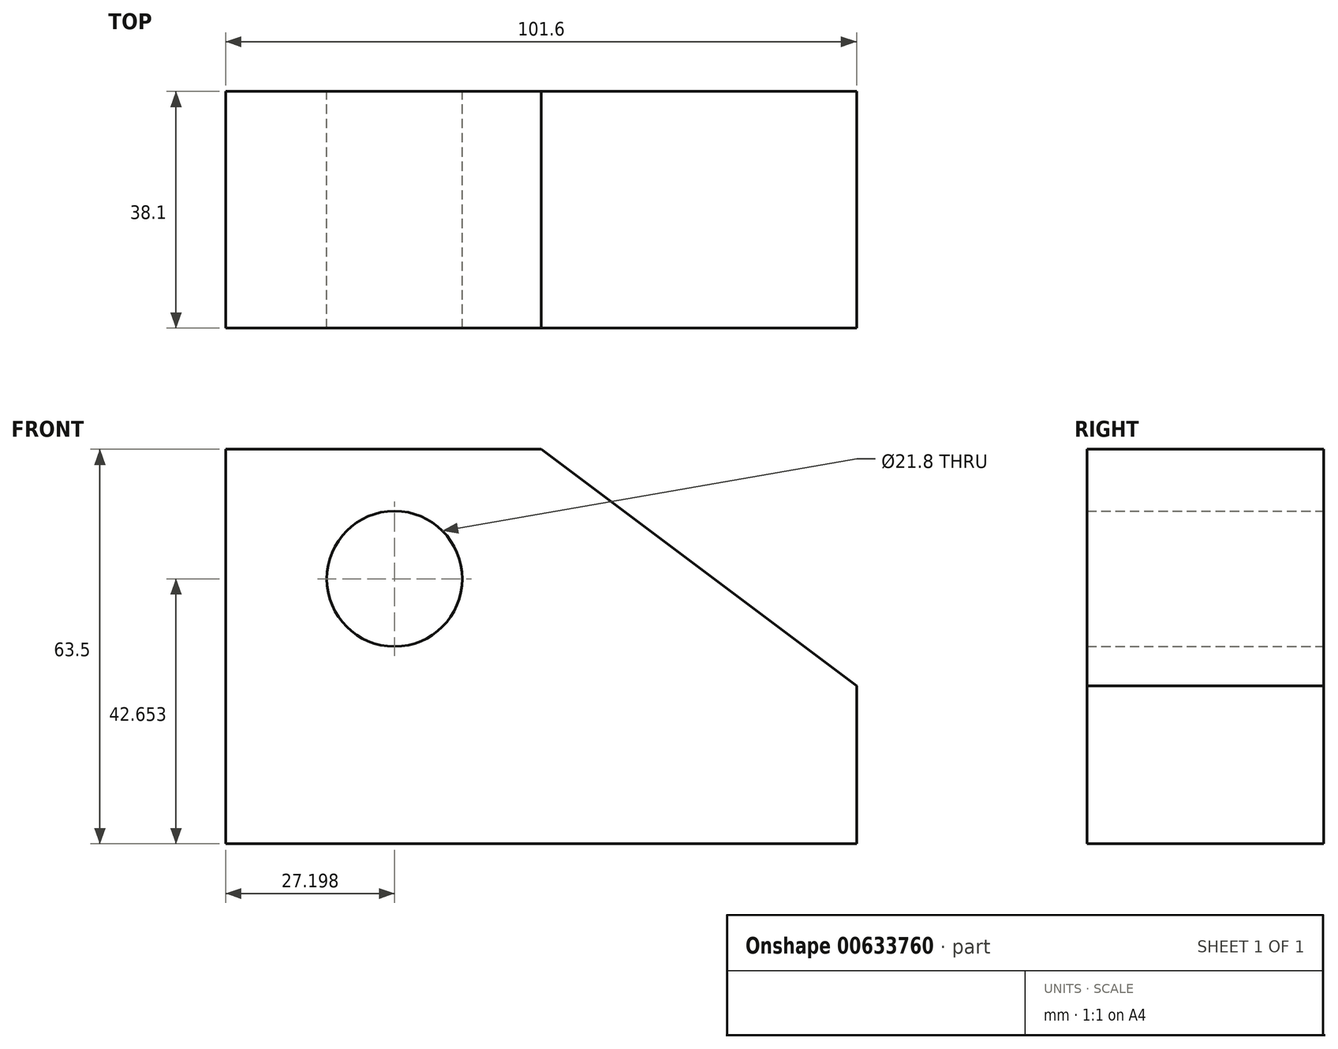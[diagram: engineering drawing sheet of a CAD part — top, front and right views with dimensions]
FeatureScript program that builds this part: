
annotation { "Feature Type Name" : "Feature", "Feature Type Description" : "" }
export const myFeature = defineFeature(function(context is Context, id is Id, definition is map)
    precondition{}
    {
        {
            var Q0;
            Q0=qCreatedBy(makeId("Front.planeOp"),FACE);
            var sketch = newSketch(context, id + "F0", { "sketchPlane" : qUnion([Q0])});
            skLineSegment(sketch, "E0", {"start": v(0, 0) * mm, "end": v(0, 63.5) * mm});
            skLineSegment(sketch, "E1", {"start": v(0, 63.5) * mm, "end": v(50.8, 63.5) * mm});
            skLineSegment(sketch, "E2", {"start": v(0, 0) * mm, "end": v(101.6, 0) * mm});
            skLineSegment(sketch, "E3", {"start": v(101.6, 0) * mm, "end": v(101.6, 25.4) * mm});
            skLineSegment(sketch, "E4", {"start": v(101.6, 25.4) * mm, "end": v(50.8, 63.5) * mm});
            skCircle(sketch, "E5", {"center": v(27.2, 42.65) * mm, "radius": 10.9 * mm});
            skSolve(sketch);
        }
        {
            var Q0;
            Q0=makeQuery(id+"F0.imprint","IMPRINT",FACE,{"disambiguationData":[TD([[makeQuery(id+"F0.imprint","IMPRINT",EDGE,{"derivedFrom":sQuery(id+"F0.wireOp",EDGE,"E0")}),-1.0]])]});
            extrude(context, id + "F1", {"entities" : qUnion([Q0]), "depth" : 38.1 * mm, "offsetDistance" : 25.4 * mm});
        }
    });
